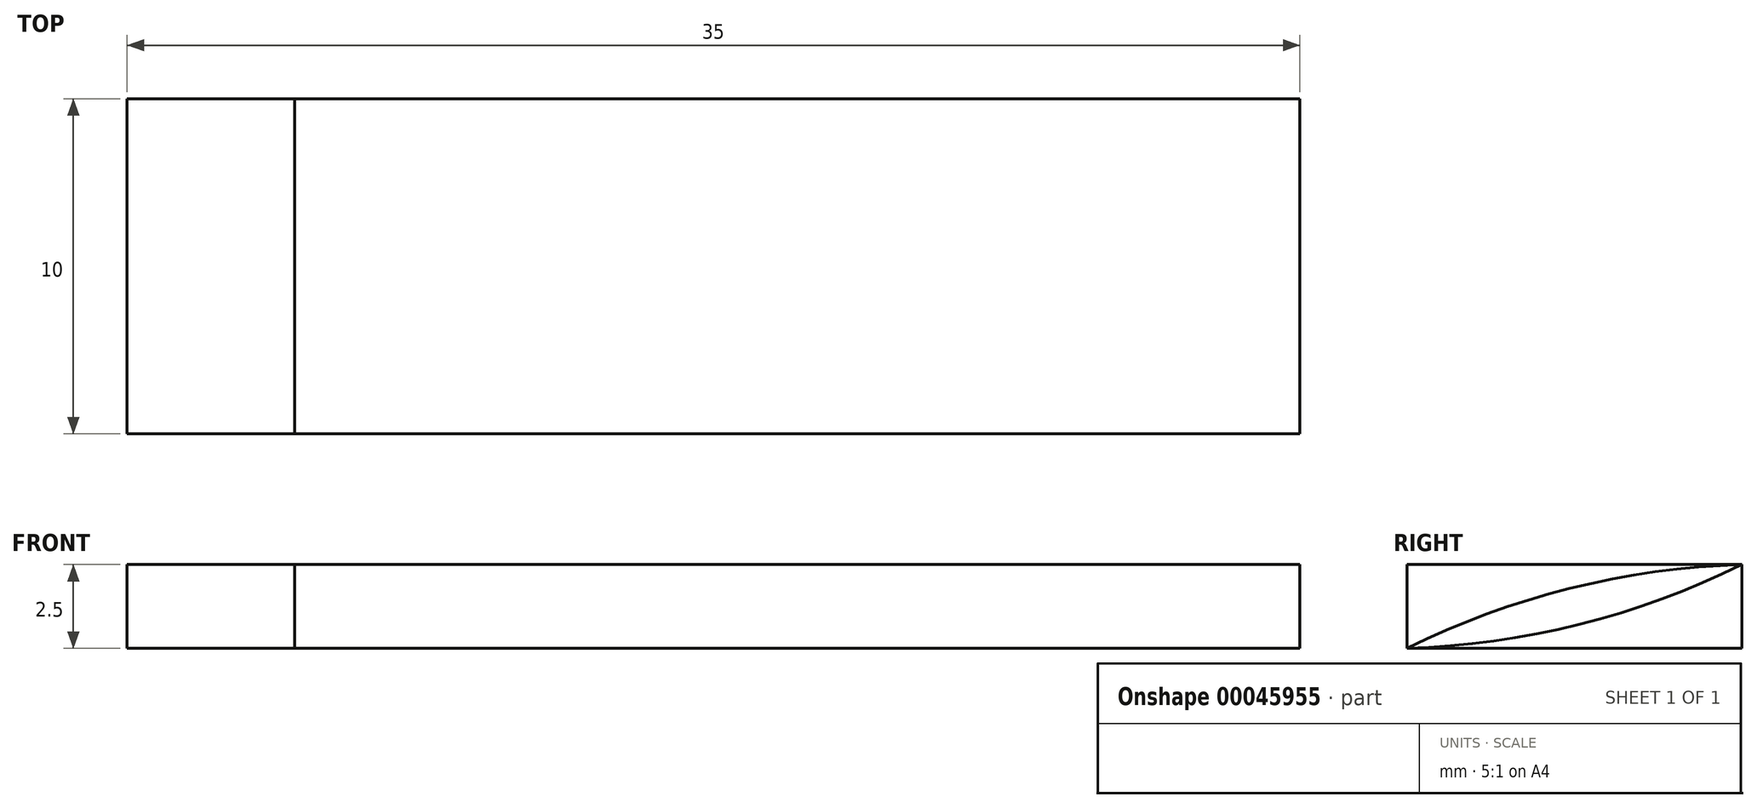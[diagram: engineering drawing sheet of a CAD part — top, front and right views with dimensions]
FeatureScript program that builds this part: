
annotation { "Feature Type Name" : "Feature", "Feature Type Description" : "" }
export const myFeature = defineFeature(function(context is Context, id is Id, definition is map)
    precondition{}
    {
        {
            var Q0;
            Q0=qCreatedBy(makeId("Top.planeOp"),FACE);
            var sketch = newSketch(context, id + "F0", { "sketchPlane" : qUnion([Q0])});
            skLineSegment(sketch, "E0.bottom", {"start": v(0, 5) * mm, "end": v(-5, 5) * mm});
            skLineSegment(sketch, "E0.top", {"start": v(0, -5) * mm, "end": v(-5, -5) * mm});
            skLineSegment(sketch, "E0.left", {"start": v(0, 5) * mm, "end": v(0, -5) * mm});
            skLineSegment(sketch, "E0.right", {"start": v(-5, 5) * mm, "end": v(-5, -5) * mm});
            skPoint(sketch, "E1", {"position": v(0, 0) * mm});
            skSolve(sketch);
        }
        {
            var Q0;
            Q0 = qSketchRegion(id + "F0", true);
            extrude(context, id + "F1", {"entities" : qUnion([Q0]), "depth" : 2.5 * mm});
        }
        {
            var Q0;
            Q0=makeQuery(id+"F1.opExtrude","SWEPT_FACE",FACE,{"disambiguationData":[OSD([sQuery(id+"F0.wireOp",EDGE,"E0.left")])]});
            var sketch = newSketch(context, id + "F2", { "sketchPlane" : qUnion([Q0])});
            skArc(sketch, "E2", {"start": v(5, 2.5) * mm, "mid": v(-0.13, 1.79) * mm, "end": v(-5, 0) * mm});
            skArc(sketch, "E3", {"start": v(-5, 0) * mm, "mid": v(0.13, 0.71) * mm, "end": v(5, 2.5) * mm});
            skSolve(sketch);
        }
        {
            var Q0;
            Q0=makeQuery(id+"F2.imprint","IMPRINT",FACE,{"disambiguationData":[TD([[makeQuery(id+"F2.imprint","IMPRINT",EDGE,{"derivedFrom":sQuery(id+"F2.wireOp",EDGE,"E2")}),1.0]])]});
            extrude(context, id + "F3", {"entities" : qUnion([Q0]), "operationType" : NewBodyOperationType.ADD, "depth" : 30 * mm});
        }
    });
